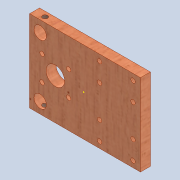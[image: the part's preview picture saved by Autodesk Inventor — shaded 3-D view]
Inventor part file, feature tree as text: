
AUTODESK INVENTOR PART (.ipt)
format: ipt  version: 2020 (Build 240168000, 168)  size: 210,432 bytes
history: native  units: mm
features: sketch x7, other x6, extrude x4, hole x3, pattern_linear x2, reference x2, direct_edit x1, move_body x1
ambient origin geometry x8: Origin, YZ Plane, XZ Plane, XY Plane, X Axis, Y Axis, Z Axis, Center Point
bodies: Solid1 (feature_tree)
feature tree (26):
  extrude  "Extrusion1"  Depth=66.0mm
  extrude  "Extrusion4"  TaperAngle=0.0deg  [1 undecoded]
  extrude  "Extrusion5"  TaperAngle=0.0deg  [1 undecoded]
  extrude  "Extrusion6"  Depth=9.0mm
  sketch  "Sketch7"  dims[d27=8.5mm d28=9.0mm]
  hole  "Hole1"  [1 undecoded]
  direct_edit  "Direct Edit1"
  pattern_linear  "Rectangular Pattern2"  Spacing1=3.5mm  [1 undecoded]
  pattern_linear  "Rectangular Pattern3"  Spacing1=21.5mm  [1 undecoded]
  hole  "Hole2"  [1 undecoded]
  hole  "Hole3"  [1 undecoded]
  sketch  "Sketch1"  dims[d0=87.5mm d1=66.0mm]
  sketch  "Sketch4"  dims[d2=8.0mm d3=0.0mm d19=0.0mm d20=0.0mm]
  sketch  "Sketch6"  dims[d24=15.0mm d25=0.0mm d26=0.0mm]
  sketch  "Sketch8"  dims[d29=10.0mm d30=9.0mm]
  reference  "Reference7"
  reference  "Reference8"
  sketch  "Sketch10"  dims[d31=0.0mm d32=0.0mm]
  sketch  "Sketch11"  dims[d33=20.748842mm d35=3.5mm d36=21.5mm d37=20.0mm d38=4.0mm d39=5.0mm d40=15.0mm d41=5.0mm d42=15.0mm d43=3.5mm d44=6.0mm d45=4.0mm d46=2.0mm d47=90.0deg d48=8.0mm d49=20.594885mm d53=0.0mm d54=0.0mm d55=2.0mm d56=26.0mm d57=20.0mm d59=15.0mm d60=20.0mm d62=41.0mm d63=20.0mm d65=27.0mm d66=8.5mm d67=4.134mm d68=5.0mm d69=4.0mm d70=2.0mm d71=90.0deg d72=7.45mm d73=20.594885mm d74=8.5mm d75=4.134mm d76=5.0mm d77=4.0mm d78=2.0mm d79=90.0deg d80=7.45mm d81=20.594885mm]
  parser-record x1  (decoder bookkeeping rows leaked as tree rows — omitted from the tree; the rows remain in map.json)
  other  "0005-00-02 X axis.iam"
  other  "Surub M4 saiba piulita.iam:65"
  other  "0005-10-1013 ISO 7089 - 4 - 140 HV.ipt:2"
  move_body  "Move1"
  other  "0005-10-04 Y axis and extruder.iam"
  other  "0005-10-1002  Hub.ipt:22"
note: 7 required parameter values undecoded (feature->parameter linkage not recoverable at this tier; creation-order binding heuristic only, values carry confidence <= 0.55)
note: 1 file-system path scrubbed to <path> (originals preserved in map.json)
